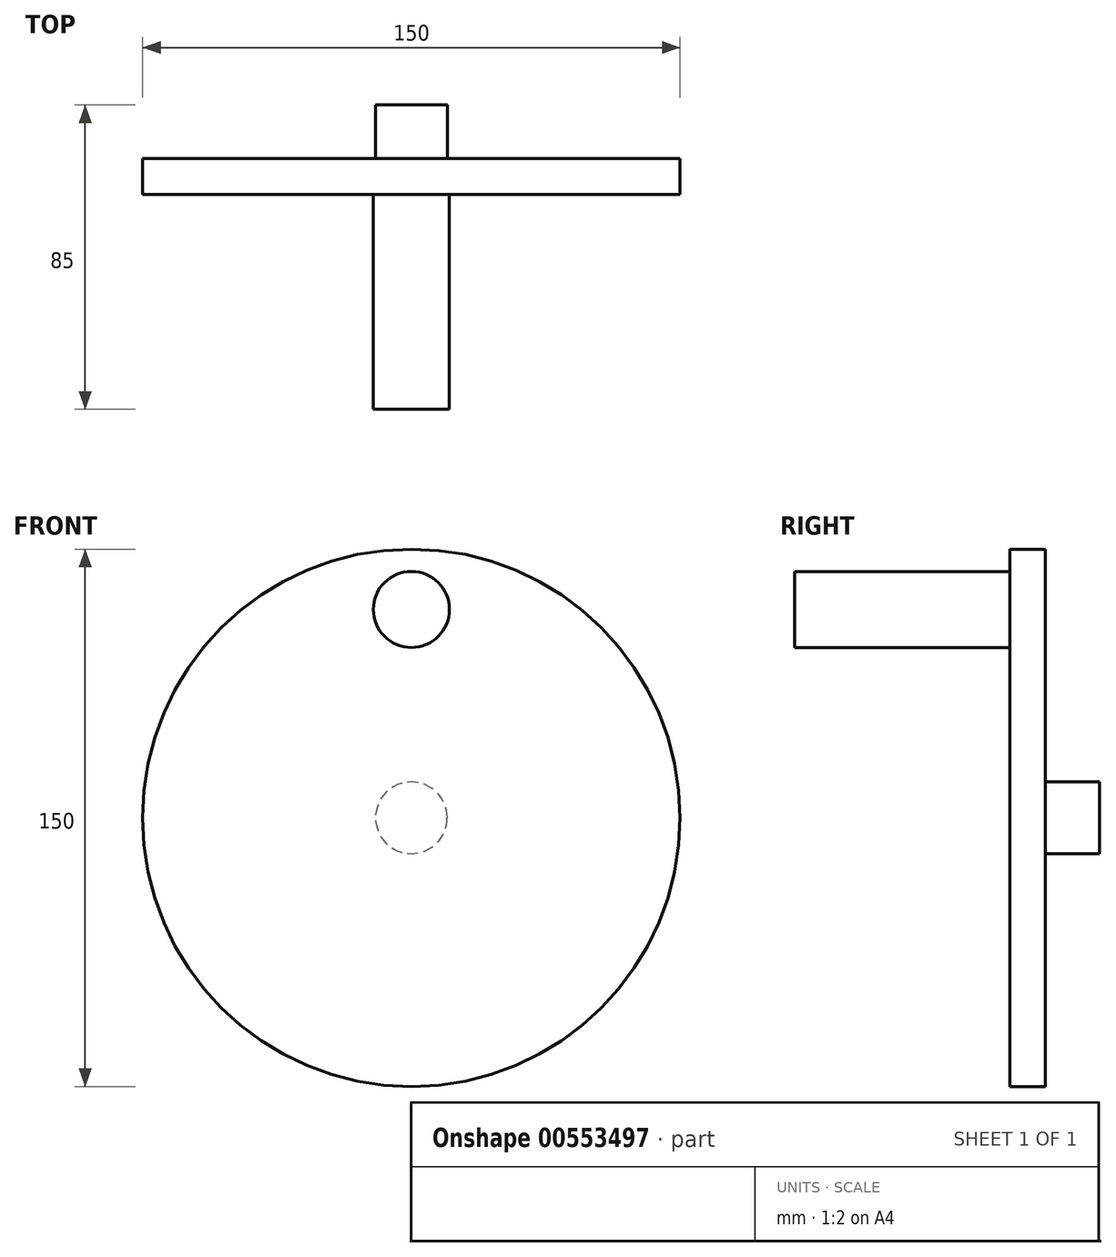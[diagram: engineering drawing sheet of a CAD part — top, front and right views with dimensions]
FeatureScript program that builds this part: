
annotation { "Feature Type Name" : "Feature", "Feature Type Description" : "" }
export const myFeature = defineFeature(function(context is Context, id is Id, definition is map)
    precondition{}
    {
        {
            var Q0;
            Q0=qCreatedBy(makeId("Front.planeOp"),FACE);
            var sketch = newSketch(context, id + "F0", { "sketchPlane" : qUnion([Q0])});
            skCircle(sketch, "E0", {"center": v(0, 0) * mm, "radius": 10 * mm});
            skSolve(sketch);
        }
        {
            var Q0;
            Q0 = qSketchRegion(id + "F0", true);
            extrude(context, id + "F1", {"entities" : qUnion([Q0]), "depth" : 15 * mm, "offsetDistance" : 25 * mm});
        }
        {
            var Q0;
            Q0=makeQuery(id+"F1.opExtrude","CAP_FACE",FACE,{"disambiguationData":[OSD([sQuery(id+"F0.wireOp",EDGE,"E0")])],"isStart":false});
            var sketch = newSketch(context, id + "F2", { "sketchPlane" : qUnion([Q0])});
            skCircle(sketch, "E1", {"center": v(0, 0) * mm, "radius": 75 * mm});
            skSolve(sketch);
        }
        {
            var Q0;
            Q0 = qSketchRegion(id + "F2", true);
            extrude(context, id + "F3", {"entities" : qUnion([Q0]), "operationType" : NewBodyOperationType.ADD, "depth" : 10 * mm, "offsetDistance" : 25 * mm});
        }
        {
            var Q0;
            Q0=makeQuery(id+"F3.opExtrude","CAP_FACE",FACE,{"disambiguationData":[OSD([sQuery(id+"F2.wireOp",EDGE,"E1")])],"isStart":false});
            var sketch = newSketch(context, id + "F4", { "sketchPlane" : qUnion([Q0])});
            skCircle(sketch, "E2", {"center": v(0, 58.15) * mm, "radius": 10.62 * mm});
            skSolve(sketch);
        }
        {
            var Q0;
            Q0 = qSketchRegion(id + "F4", true);
            extrude(context, id + "F5", {"entities" : qUnion([Q0]), "operationType" : NewBodyOperationType.ADD, "depth" : 60 * mm, "offsetDistance" : 25 * mm});
        }
    });
